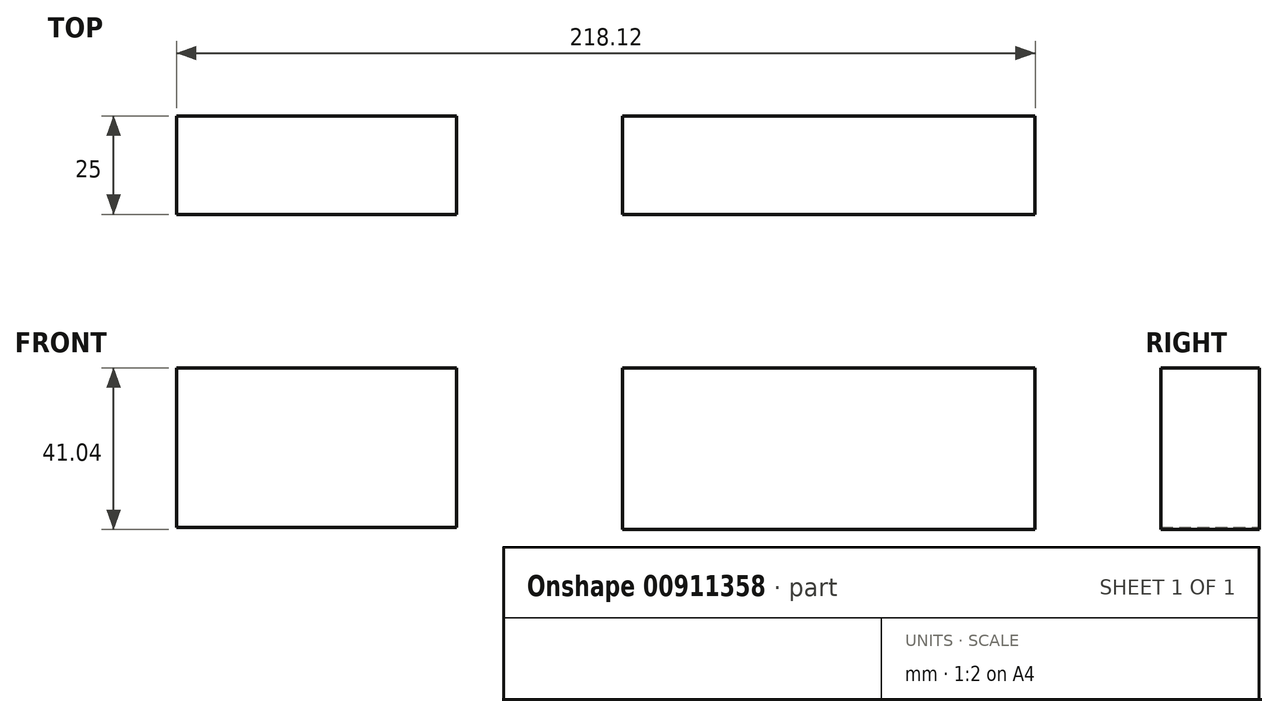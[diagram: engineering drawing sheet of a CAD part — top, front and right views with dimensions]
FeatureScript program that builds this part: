
annotation { "Feature Type Name" : "Feature", "Feature Type Description" : "" }
export const myFeature = defineFeature(function(context is Context, id is Id, definition is map)
    precondition{}
    {
        {
            var Q0;
            Q0=qCreatedBy(makeId("Front.planeOp"),FACE);
            var sketch = newSketch(context, id + "F0", { "sketchPlane" : qUnion([Q0])});
            skLineSegment(sketch, "E0.bottom", {"start": v(-27.97, 48.77) * mm, "end": v(-99.08, 48.77) * mm});
            skLineSegment(sketch, "E0.top", {"start": v(-27.97, 8.3) * mm, "end": v(-99.08, 8.3) * mm});
            skLineSegment(sketch, "E0.left", {"start": v(-27.97, 48.77) * mm, "end": v(-27.97, 8.3) * mm});
            skLineSegment(sketch, "E0.right", {"start": v(-99.08, 48.77) * mm, "end": v(-99.08, 8.3) * mm});
            skLineSegment(sketch, "E1.bottom", {"start": v(14.2, 48.77) * mm, "end": v(119.04, 48.77) * mm});
            skLineSegment(sketch, "E1.top", {"start": v(14.2, 7.73) * mm, "end": v(119.04, 7.73) * mm});
            skLineSegment(sketch, "E1.left", {"start": v(14.2, 48.77) * mm, "end": v(14.2, 7.73) * mm});
            skLineSegment(sketch, "E1.right", {"start": v(119.04, 48.77) * mm, "end": v(119.04, 7.73) * mm});
            skSolve(sketch);
        }
        {
            var Q0;
            Q0=makeQuery(id+"F0.imprint","IMPRINT",FACE,{"disambiguationData":[TD([[makeQuery(id+"F0.imprint","IMPRINT",EDGE,{"derivedFrom":sQuery(id+"F0.wireOp",EDGE,"E0.bottom")}),1.0]])]});
            var Q1;
            Q1=makeQuery(id+"F0.imprint","IMPRINT",FACE,{"disambiguationData":[TD([[makeQuery(id+"F0.imprint","IMPRINT",EDGE,{"derivedFrom":sQuery(id+"F0.wireOp",EDGE,"E1.bottom")}),-1.0]])]});
            extrude(context, id + "F1", {"entities" : qUnion([Q0, Q1]), "depth" : 25 * mm, "offsetDistance" : 25 * mm});
        }
    });
